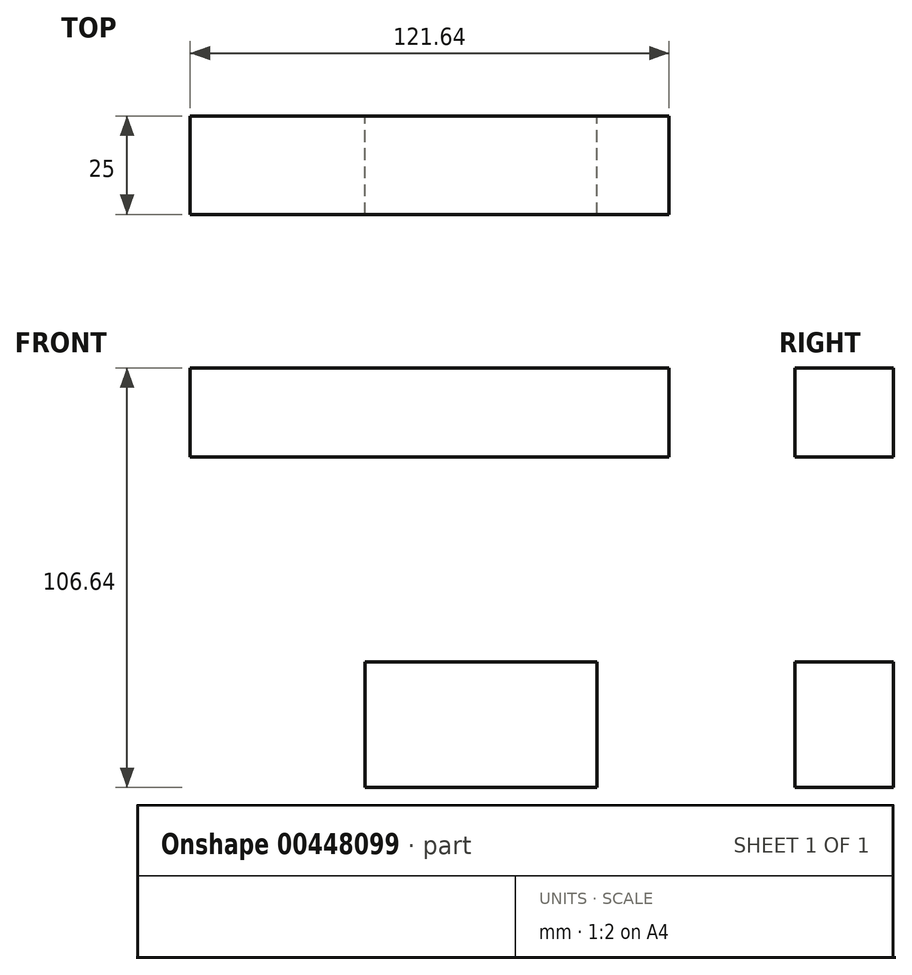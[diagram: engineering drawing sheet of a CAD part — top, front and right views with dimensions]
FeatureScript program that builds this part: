
annotation { "Feature Type Name" : "Feature", "Feature Type Description" : "" }
export const myFeature = defineFeature(function(context is Context, id is Id, definition is map)
    precondition{}
    {
        {
            var Q0;
            Q0=qCreatedBy(makeId("Front.planeOp"),FACE);
            var sketch = newSketch(context, id + "F0", { "sketchPlane" : qUnion([Q0])});
            skLineSegment(sketch, "E0.bottom", {"start": v(59.02, 31.95) * mm, "end": v(0, 31.95) * mm});
            skLineSegment(sketch, "E0.top", {"start": v(59.02, 0) * mm, "end": v(0, 0) * mm});
            skLineSegment(sketch, "E0.left", {"start": v(59.02, 31.95) * mm, "end": v(59.02, 0) * mm});
            skLineSegment(sketch, "E0.right", {"start": v(0, 31.95) * mm, "end": v(0, 0) * mm});
            skLineSegment(sketch, "E1.bottom", {"start": v(77.26, 83.95) * mm, "end": v(-44.38, 83.95) * mm});
            skLineSegment(sketch, "E1.top", {"start": v(77.26, 106.64) * mm, "end": v(-44.38, 106.64) * mm});
            skLineSegment(sketch, "E1.left", {"start": v(77.26, 83.95) * mm, "end": v(77.26, 106.64) * mm});
            skLineSegment(sketch, "E1.right", {"start": v(-44.38, 83.95) * mm, "end": v(-44.38, 106.64) * mm});
            skLineSegment(sketch, "E2.bottom", {"start": v(-14.92, 83.95) * mm, "end": v(-44.38, 83.95) * mm, "construction": true});
            skLineSegment(sketch, "E2.top", {"start": v(-14.92, 83.95) * mm, "end": v(-44.38, 83.95) * mm, "construction": true});
            skLineSegment(sketch, "E2.left", {"start": v(-14.92, 83.95) * mm, "end": v(-14.92, 83.95) * mm});
            skLineSegment(sketch, "E2.right", {"start": v(-44.38, 83.95) * mm, "end": v(-44.38, 83.95) * mm});
            skSolve(sketch);
        }
        {
            var Q0;
            Q0 = qSketchRegion(id + "F0", true);
            extrude(context, id + "F1", {"entities" : qUnion([Q0]), "depth" : 25 * mm});
        }
    });
